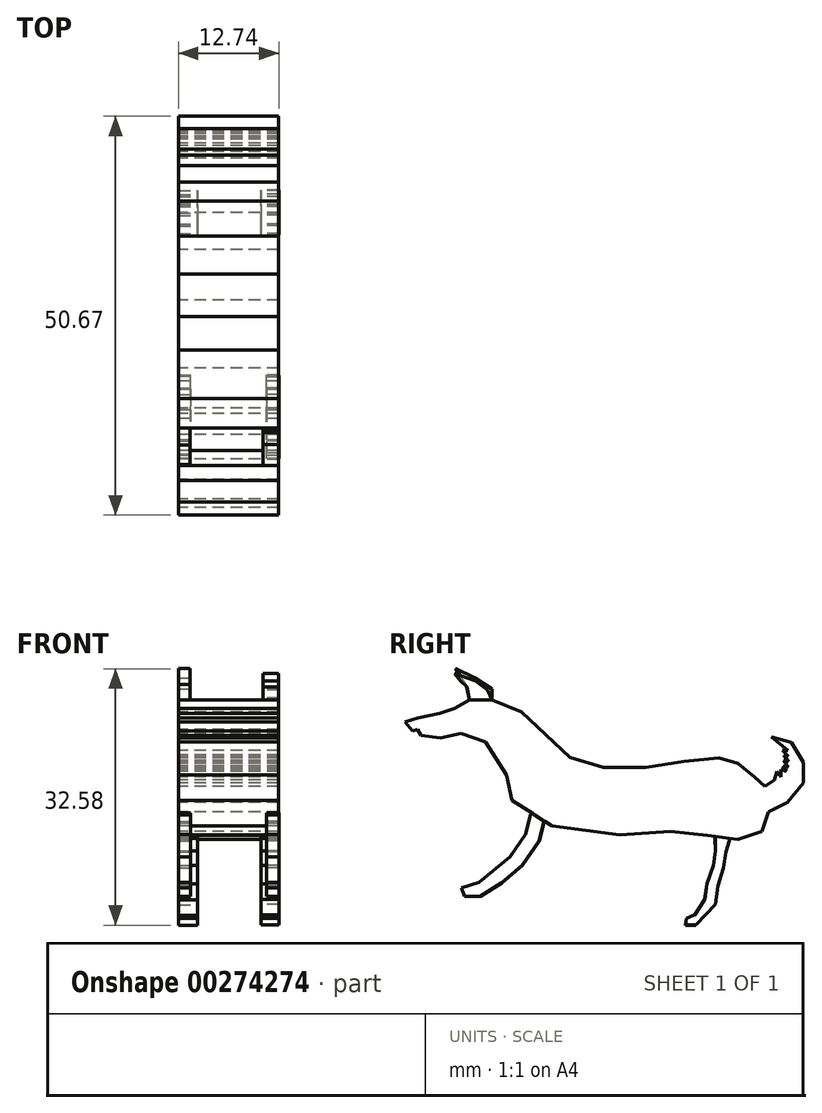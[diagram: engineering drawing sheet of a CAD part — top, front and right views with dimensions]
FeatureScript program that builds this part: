
annotation { "Feature Type Name" : "Feature", "Feature Type Description" : "" }
export const myFeature = defineFeature(function(context is Context, id is Id, definition is map)
    precondition{}
    {
        {
            var Q0;
            Q0=qCreatedBy(makeId("Right.planeOp"),FACE);
            var sketch = newSketch(context, id + "F0", { "sketchPlane" : qUnion([Q0])});
            skLineSegment(sketch, "E0", {"start": v(-9.66, 15.32) * mm, "end": v(-15.82, 21.1) * mm});
            skLineSegment(sketch, "E1", {"start": v(-15.82, 21.1) * mm, "end": v(-19.56, 22.63) * mm});
            skLineSegment(sketch, "E2", {"start": v(-22.42, 22.63) * mm, "end": v(-24.34, 21.56) * mm});
            skLineSegment(sketch, "E3", {"start": v(-24.34, 21.56) * mm, "end": v(-26.22, 20.93) * mm});
            skLineSegment(sketch, "E4", {"start": v(-26.22, 20.93) * mm, "end": v(-28.98, 20.37) * mm});
            skLineSegment(sketch, "E5", {"start": v(-28.98, 20.37) * mm, "end": v(-30.64, 19.86) * mm});
            skLineSegment(sketch, "E6", {"start": v(-30.64, 19.86) * mm, "end": v(-29.67, 18.72) * mm});
            skLineSegment(sketch, "E7", {"start": v(-29.67, 18.72) * mm, "end": v(-27.26, 19.22) * mm});
            skLineSegment(sketch, "E8", {"start": v(-27.26, 19.22) * mm, "end": v(-29, 18.85) * mm});
            skLineSegment(sketch, "E9", {"start": v(-29, 18.85) * mm, "end": v(-28.6, 18.11) * mm});
            skLineSegment(sketch, "E10", {"start": v(-28.6, 18.11) * mm, "end": v(-26.1, 17.83) * mm});
            skLineSegment(sketch, "E11", {"start": v(-26.1, 17.83) * mm, "end": v(-23.52, 18.38) * mm});
            skLineSegment(sketch, "E12", {"start": v(-23.52, 18.38) * mm, "end": v(-20.38, 17.27) * mm});
            skLineSegment(sketch, "E13", {"start": v(-20.38, 17.27) * mm, "end": v(-17.7, 13.09) * mm});
            skLineSegment(sketch, "E14", {"start": v(-17.7, 13.09) * mm, "end": v(-17.02, 9.88) * mm});
            skLineSegment(sketch, "E15", {"start": v(-17.02, 9.88) * mm, "end": v(-11.93, 6.63) * mm});
            skLineSegment(sketch, "E16", {"start": v(-11.93, 6.63) * mm, "end": v(-3.3, 5.48) * mm});
            skLineSegment(sketch, "E17", {"start": v(-3.3, 5.48) * mm, "end": v(3.1, 5.94) * mm});
            skLineSegment(sketch, "E18", {"start": v(3.1, 5.94) * mm, "end": v(7.78, 5.46) * mm});
            skLineSegment(sketch, "E19", {"start": v(7.78, 5.46) * mm, "end": v(11.67, 4.93) * mm});
            skLineSegment(sketch, "E20", {"start": v(11.67, 4.93) * mm, "end": v(14.7, 5.94) * mm});
            skLineSegment(sketch, "E21", {"start": v(14.7, 5.94) * mm, "end": v(15.56, 8.39) * mm});
            skLineSegment(sketch, "E22", {"start": v(15.56, 8.39) * mm, "end": v(17.97, 9.63) * mm});
            skLineSegment(sketch, "E23", {"start": v(17.97, 9.63) * mm, "end": v(20.03, 12.08) * mm});
            skLineSegment(sketch, "E24", {"start": v(20.03, 12.08) * mm, "end": v(20.03, 14.68) * mm});
            skLineSegment(sketch, "E25", {"start": v(20.03, 14.68) * mm, "end": v(18.45, 17.22) * mm});
            skLineSegment(sketch, "E26", {"start": v(18.45, 17.22) * mm, "end": v(15.9, 17.94) * mm});
            skLineSegment(sketch, "E27", {"start": v(15.9, 17.94) * mm, "end": v(18.01, 16.21) * mm});
            skLineSegment(sketch, "E28", {"start": v(18.01, 16.21) * mm, "end": v(17.35, 16.21) * mm});
            skLineSegment(sketch, "E29", {"start": v(17.35, 16.21) * mm, "end": v(18.12, 15.47) * mm});
            skLineSegment(sketch, "E30", {"start": v(18.12, 15.47) * mm, "end": v(17.54, 15.64) * mm});
            skLineSegment(sketch, "E31", {"start": v(17.54, 15.64) * mm, "end": v(18.12, 14.79) * mm});
            skLineSegment(sketch, "E32", {"start": v(18.12, 14.79) * mm, "end": v(17.46, 14.97) * mm});
            skLineSegment(sketch, "E33", {"start": v(17.46, 14.97) * mm, "end": v(18.09, 14.05) * mm});
            skLineSegment(sketch, "E34", {"start": v(18.09, 14.05) * mm, "end": v(17.4, 14.25) * mm});
            skLineSegment(sketch, "E35", {"start": v(17.4, 14.25) * mm, "end": v(17.85, 13.58) * mm});
            skLineSegment(sketch, "E36", {"start": v(17.85, 13.58) * mm, "end": v(17.12, 13.78) * mm});
            skLineSegment(sketch, "E37", {"start": v(17.12, 13.78) * mm, "end": v(17.12, 12.85) * mm});
            skLineSegment(sketch, "E38", {"start": v(17.12, 12.85) * mm, "end": v(16.63, 13.58) * mm});
            skLineSegment(sketch, "E39", {"start": v(16.63, 13.58) * mm, "end": v(16.31, 12.47) * mm});
            skLineSegment(sketch, "E40", {"start": v(16.31, 12.47) * mm, "end": v(15.9, 12.19) * mm});
            skLineSegment(sketch, "E41", {"start": v(15.9, 12.19) * mm, "end": v(15.12, 11.66) * mm});
            skLineSegment(sketch, "E42", {"start": v(15.12, 11.66) * mm, "end": v(13.8, 12.85) * mm});
            skLineSegment(sketch, "E43", {"start": v(13.8, 12.85) * mm, "end": v(11.66, 14.58) * mm});
            skLineSegment(sketch, "E44", {"start": v(11.66, 14.58) * mm, "end": v(9.24, 15.27) * mm});
            skLineSegment(sketch, "E45", {"start": v(9.24, 15.27) * mm, "end": v(4.8, 14.83) * mm});
            skLineSegment(sketch, "E46", {"start": v(4.8, 14.83) * mm, "end": v(0, 14.05) * mm});
            skLineSegment(sketch, "E47", {"start": v(0, 14.05) * mm, "end": v(-5.43, 14.05) * mm});
            skLineSegment(sketch, "E48", {"start": v(-5.43, 14.05) * mm, "end": v(-9.66, 15.32) * mm});
            skLineSegment(sketch, "E49", {"start": v(-19.56, 22.63) * mm, "end": v(-22.42, 22.63) * mm});
            skSolve(sketch);
        }
        {
            var Q0;
            Q0 = qSketchRegion(id + "F0", true);
            extrude(context, id + "F1", {"entities" : qUnion([Q0]), "depth" : 12.7 * mm, "offsetDistance" : 25.4 * mm});
        }
        {
            var Q0;
            Q0=makeQuery(id+"F1.opExtrude","SWEPT_FACE",FACE,{"disambiguationData":[OSD([sQuery(id+"F0.wireOp",EDGE,"E49")])]});
            var sketch = newSketch(context, id + "F2", { "sketchPlane" : qUnion([Q0])});
            skLineSegment(sketch, "E50.bottom", {"start": v(12.7, -19.56) * mm, "end": v(10.72, -19.56) * mm});
            skLineSegment(sketch, "E50.top", {"start": v(12.7, -22.42) * mm, "end": v(10.72, -22.42) * mm});
            skLineSegment(sketch, "E50.left", {"start": v(12.7, -19.56) * mm, "end": v(12.7, -22.42) * mm});
            skLineSegment(sketch, "E50.right", {"start": v(10.72, -19.56) * mm, "end": v(10.72, -22.42) * mm});
            skPoint(sketch, "E50.middle", {"position": v(11.7, -21) * mm});
            skPoint(sketch, "E50.middle.positionSnap0", {"position": v(12.7, -21) * mm});
            skPoint(sketch, "E50.centerSnap0", {"position": v(12.7, -21) * mm});
            skLineSegment(sketch, "E51.bottom", {"start": v(1.44, -19.56) * mm, "end": v(0.01, -19.56) * mm});
            skLineSegment(sketch, "E51.top", {"start": v(1.44, -22.42) * mm, "end": v(0.01, -22.42) * mm});
            skLineSegment(sketch, "E51.left", {"start": v(1.44, -19.56) * mm, "end": v(1.44, -22.42) * mm});
            skLineSegment(sketch, "E51.right", {"start": v(0.01, -19.56) * mm, "end": v(0.01, -22.42) * mm});
            skPoint(sketch, "E51.middle", {"position": v(0.72, -21) * mm});
            skPoint(sketch, "E51.middle.positionSnap0", {"position": v(0, -21) * mm});
            skPoint(sketch, "E51.centerSnap0", {"position": v(0, -21) * mm});
            skSolve(sketch);
        }
        {
            var Q0;
            Q0 = qSketchRegion(id + "F2", true);
            extrude(context, id + "F3", {"entities" : qUnion([Q0]), "operationType" : NewBodyOperationType.ADD, "depth" : 0.25 * mm, "offsetDistance" : 25.4 * mm});
        }
        {
            var Q0;
            Q0=makeQuery(id+"F3.opExtrude","SWEPT_FACE",FACE,{"disambiguationData":[OSD([sQuery(id+"F2.wireOp",EDGE,"E50.right")])]});
            var sketch = newSketch(context, id + "F4", { "sketchPlane" : qUnion([Q0])});
            skLineSegment(sketch, "E52", {"start": v(22.42, 22.63) * mm, "end": v(22.76, 24.29) * mm});
            skLineSegment(sketch, "E53", {"start": v(22.76, 24.29) * mm, "end": v(23.56, 25.07) * mm});
            skLineSegment(sketch, "E54", {"start": v(23.56, 25.07) * mm, "end": v(24.36, 25.99) * mm});
            skLineSegment(sketch, "E55", {"start": v(24.36, 25.99) * mm, "end": v(21.67, 25.07) * mm});
            skLineSegment(sketch, "E56", {"start": v(21.67, 25.07) * mm, "end": v(20.12, 23.91) * mm});
            skLineSegment(sketch, "E57", {"start": v(20.12, 23.91) * mm, "end": v(19.56, 22.63) * mm});
            skLineSegment(sketch, "E58", {"start": v(19.56, 22.63) * mm, "end": v(22.42, 22.63) * mm});
            skSolve(sketch);
        }
        {
            var Q0;
            Q0 = qSketchRegion(id + "F4", true);
            extrude(context, id + "F5", {"entities" : qUnion([Q0]), "operationType" : NewBodyOperationType.ADD, "oppositeDirection" : true, "depth" : 2 * mm, "offsetDistance" : 25.4 * mm});
        }
        {
            var Q0;
            Q0=makeQuery(id+"F3.opExtrude","SWEPT_FACE",FACE,{"disambiguationData":[OSD([sQuery(id+"F2.wireOp",EDGE,"E51.left")])]});
            var sketch = newSketch(context, id + "F6", { "sketchPlane" : qUnion([Q0])});
            skLineSegment(sketch, "E59", {"start": v(-19.56, 22.63) * mm, "end": v(-22.42, 22.63) * mm});
            skLineSegment(sketch, "E60", {"start": v(-22.42, 22.63) * mm, "end": v(-22.85, 24.57) * mm});
            skLineSegment(sketch, "E61", {"start": v(-22.85, 24.57) * mm, "end": v(-24.21, 26.6) * mm});
            skLineSegment(sketch, "E62", {"start": v(-24.21, 26.6) * mm, "end": v(-21.7, 25.42) * mm});
            skLineSegment(sketch, "E63", {"start": v(-21.7, 25.42) * mm, "end": v(-19.56, 24.02) * mm});
            skLineSegment(sketch, "E64", {"start": v(-19.56, 24.02) * mm, "end": v(-19.56, 22.63) * mm});
            skSolve(sketch);
        }
        {
            var Q0;
            Q0 = qSketchRegion(id + "F6", true);
            extrude(context, id + "F7", {"entities" : qUnion([Q0]), "operationType" : NewBodyOperationType.ADD, "oppositeDirection" : true, "depth" : 1.45 * mm, "offsetDistance" : 25.4 * mm});
        }
        {
            var Q0;
            Q0=makeQuery(id+"F1.opExtrude","SWEPT_FACE",FACE,{"disambiguationData":[OSD([sQuery(id+"F0.wireOp",EDGE,"E15")])]});
            var sketch = newSketch(context, id + "F8", { "sketchPlane" : qUnion([Q0])});
            skLineSegment(sketch, "E65.bottom", {"start": v(12.7, 16.64) * mm, "end": v(11.16, 16.64) * mm});
            skLineSegment(sketch, "E65.top", {"start": v(12.7, 14.69) * mm, "end": v(11.16, 14.69) * mm});
            skLineSegment(sketch, "E65.left", {"start": v(12.7, 16.64) * mm, "end": v(12.7, 14.69) * mm});
            skLineSegment(sketch, "E65.right", {"start": v(11.16, 16.64) * mm, "end": v(11.16, 14.69) * mm});
            skPoint(sketch, "E65.middle", {"position": v(11.93, 15.66) * mm});
            skLineSegment(sketch, "E66.bottom", {"start": v(0, 16.64) * mm, "end": v(2.4, 16.64) * mm});
            skLineSegment(sketch, "E66.top", {"start": v(0, 14.69) * mm, "end": v(2.4, 14.69) * mm});
            skLineSegment(sketch, "E66.left", {"start": v(0, 16.64) * mm, "end": v(0, 14.69) * mm});
            skLineSegment(sketch, "E66.right", {"start": v(1.52, 16.64) * mm, "end": v(1.52, 14.69) * mm});
            skPoint(sketch, "E66.middle", {"position": v(1.2, 15.66) * mm});
            skPoint(sketch, "E66.middle.positionSnap0", {"position": v(11.16, 15.66) * mm});
            skPoint(sketch, "E66.centerSnap0", {"position": v(11.16, 15.66) * mm});
            skSolve(sketch);
        }
        {
            var Q0;
            Q0 = qSketchRegion(id + "F8", true);
            extrude(context, id + "F9", {"entities" : qUnion([Q0]), "operationType" : NewBodyOperationType.ADD, "depth" : 0.25 * mm, "offsetDistance" : 25.4 * mm});
        }
        {
            var Q0;
            Q0=makeQuery(id+"F9.opExtrude","SWEPT_FACE",FACE,{"disambiguationData":[OSD([sQuery(id+"F8.wireOp",EDGE,"E66.right")])]});
            var sketch = newSketch(context, id + "F10", { "sketchPlane" : qUnion([Q0])});
            skLineSegment(sketch, "E67", {"start": v(-14.47, 8.25) * mm, "end": v(-12.82, 7.2) * mm});
            skLineSegment(sketch, "E68", {"start": v(-12.82, 7.2) * mm, "end": v(-12.96, 6.99) * mm});
            skLineSegment(sketch, "E69", {"start": v(-12.96, 6.99) * mm, "end": v(-14.61, 8.04) * mm});
            skLineSegment(sketch, "E70", {"start": v(-14.61, 8.04) * mm, "end": v(-14.47, 8.25) * mm});
            skLineSegment(sketch, "E71", {"start": v(-14.61, 8.04) * mm, "end": v(-15.29, 5.55) * mm});
            skLineSegment(sketch, "E72", {"start": v(-15.29, 5.55) * mm, "end": v(-17.25, 2.7) * mm});
            skLineSegment(sketch, "E73", {"start": v(-17.25, 2.7) * mm, "end": v(-19.58, 0.79) * mm});
            skLineSegment(sketch, "E74", {"start": v(-23.38, -1.23) * mm, "end": v(-22.99, -2.34) * mm});
            skLineSegment(sketch, "E75", {"start": v(-22.99, -2.34) * mm, "end": v(-21.03, -2.34) * mm});
            skLineSegment(sketch, "E76", {"start": v(-21.03, -2.34) * mm, "end": v(-18.32, -0.58) * mm});
            skLineSegment(sketch, "E77", {"start": v(-18.32, -0.58) * mm, "end": v(-15.72, 1.64) * mm});
            skLineSegment(sketch, "E78", {"start": v(-15.72, 1.64) * mm, "end": v(-13.54, 4.71) * mm});
            skLineSegment(sketch, "E79", {"start": v(-13.54, 4.71) * mm, "end": v(-12.96, 6.99) * mm});
            skLineSegment(sketch, "E80", {"start": v(-19.58, 0.79) * mm, "end": v(-21.2, -0.55) * mm});
            skLineSegment(sketch, "E81", {"start": v(-21.2, -0.55) * mm, "end": v(-23.38, -1.23) * mm});
            skSolve(sketch);
        }
        {
            var Q0;
            Q0 = qSketchRegion(id + "F10", true);
            extrude(context, id + "F11", {"entities" : qUnion([Q0]), "operationType" : NewBodyOperationType.ADD, "oppositeDirection" : true, "depth" : 1.52 * mm, "offsetDistance" : 25.4 * mm});
        }
        {
            var Q0;
            Q0=makeQuery(id+"F9.opExtrude","SWEPT_FACE",FACE,{"disambiguationData":[OSD([sQuery(id+"F8.wireOp",EDGE,"E65.right")])]});
            var sketch = newSketch(context, id + "F12", { "sketchPlane" : qUnion([Q0])});
            skLineSegment(sketch, "E82.MirrorCS", {"start": v(12.87, 7.2) * mm, "end": v(13, 6.99) * mm});
            skLineSegment(sketch, "E83.MirrorCS", {"start": v(14.66, 8.04) * mm, "end": v(14.52, 8.25) * mm});
            skLineSegment(sketch, "E84.MirrorCS", {"start": v(23.43, -1.24) * mm, "end": v(23.03, -2.34) * mm});
            skLineSegment(sketch, "E85.MirrorCS", {"start": v(14.52, 8.25) * mm, "end": v(12.87, 7.2) * mm});
            skLineSegment(sketch, "E86.MirrorCS", {"start": v(13, 6.99) * mm, "end": v(14.66, 8.04) * mm});
            skLineSegment(sketch, "E87.MirrorCS", {"start": v(14.66, 8.04) * mm, "end": v(15.33, 5.55) * mm});
            skLineSegment(sketch, "E88.MirrorCS", {"start": v(15.33, 5.55) * mm, "end": v(17.3, 2.7) * mm});
            skLineSegment(sketch, "E89.MirrorCS", {"start": v(17.3, 2.7) * mm, "end": v(19.63, 0.78) * mm});
            skLineSegment(sketch, "E90.MirrorCS", {"start": v(23.03, -2.34) * mm, "end": v(21.07, -2.34) * mm});
            skLineSegment(sketch, "E91.MirrorCS", {"start": v(21.07, -2.34) * mm, "end": v(18.37, -0.59) * mm});
            skLineSegment(sketch, "E92.MirrorCS", {"start": v(18.37, -0.59) * mm, "end": v(15.76, 1.64) * mm});
            skLineSegment(sketch, "E93.MirrorCS", {"start": v(15.76, 1.64) * mm, "end": v(13.58, 4.7) * mm});
            skLineSegment(sketch, "E94.MirrorCS", {"start": v(13.58, 4.7) * mm, "end": v(13, 6.99) * mm});
            skLineSegment(sketch, "E95.MirrorCS", {"start": v(21.24, -0.55) * mm, "end": v(23.43, -1.24) * mm});
            skLineSegment(sketch, "E96.MirrorCS", {"start": v(19.63, 0.78) * mm, "end": v(21.24, -0.55) * mm});
            skSolve(sketch);
        }
        {
            var Q0;
            Q0 = qSketchRegion(id + "F12", true);
            extrude(context, id + "F13", {"entities" : qUnion([Q0]), "operationType" : NewBodyOperationType.ADD, "oppositeDirection" : true, "depth" : 1.57 * mm, "offsetDistance" : 25.4 * mm});
        }
        {
            var Q0;
            Q0=makeQuery(id+"F1.opExtrude","SWEPT_FACE",FACE,{"disambiguationData":[OSD([sQuery(id+"F0.wireOp",EDGE,"E19")])]});
            var sketch = newSketch(context, id + "F14", { "sketchPlane" : qUnion([Q0])});
            skLineSegment(sketch, "E97.bottom", {"start": v(12.7, -9.85) * mm, "end": v(10.44, -9.85) * mm});
            skLineSegment(sketch, "E97.top", {"start": v(12.7, -8.03) * mm, "end": v(10.44, -8.03) * mm});
            skLineSegment(sketch, "E97.left", {"start": v(12.7, -9.85) * mm, "end": v(12.7, -8.03) * mm});
            skLineSegment(sketch, "E97.right", {"start": v(10.44, -9.85) * mm, "end": v(10.44, -8.03) * mm});
            skPoint(sketch, "E97.middle", {"position": v(11.57, -8.94) * mm});
            skPoint(sketch, "E97.middle.positionSnap0", {"position": v(12.7, -8.94) * mm});
            skPoint(sketch, "E97.centerSnap0", {"position": v(12.7, -8.94) * mm});
            skLineSegment(sketch, "E98.bottom", {"start": v(0, -9.83) * mm, "end": v(2.43, -9.83) * mm});
            skLineSegment(sketch, "E98.top", {"start": v(0, -8.05) * mm, "end": v(2.43, -8.05) * mm});
            skLineSegment(sketch, "E98.left", {"start": v(0, -9.83) * mm, "end": v(0, -8.05) * mm});
            skLineSegment(sketch, "E98.right", {"start": v(2.43, -9.83) * mm, "end": v(2.43, -8.05) * mm});
            skPoint(sketch, "E98.middle", {"position": v(1.21, -8.94) * mm});
            skPoint(sketch, "E98.middle.positionSnap0", {"position": v(0, -8.94) * mm});
            skPoint(sketch, "E98.centerSnap0", {"position": v(0, -8.94) * mm});
            skSolve(sketch);
        }
        {
            var Q0;
            Q0 = qSketchRegion(id + "F14", true);
            extrude(context, id + "F15", {"entities" : qUnion([Q0]), "operationType" : NewBodyOperationType.ADD, "depth" : 0.25 * mm, "offsetDistance" : 25.4 * mm});
        }
        {
            var Q0;
            Q0=makeQuery(id+"F15.opExtrude","SWEPT_FACE",FACE,{"disambiguationData":[OSD([sQuery(id+"F14.wireOp",EDGE,"E97.right")])]});
            var sketch = newSketch(context, id + "F16", { "sketchPlane" : qUnion([Q0])});
            skLineSegment(sketch, "E99", {"start": v(-8.8, 5.06) * mm, "end": v(-8.83, 5.31) * mm});
            skLineSegment(sketch, "E100", {"start": v(-8.83, 5.31) * mm, "end": v(-10.63, 5.07) * mm});
            skLineSegment(sketch, "E101", {"start": v(-10.63, 5.07) * mm, "end": v(-10.6, 4.82) * mm});
            skLineSegment(sketch, "E102", {"start": v(-10.6, 4.82) * mm, "end": v(-8.8, 5.06) * mm});
            skLineSegment(sketch, "E103", {"start": v(-8.8, 5.06) * mm, "end": v(-8.83, 3.48) * mm});
            skLineSegment(sketch, "E104", {"start": v(-8.83, 3.48) * mm, "end": v(-8.58, 1.63) * mm});
            skLineSegment(sketch, "E105", {"start": v(-8.58, 1.63) * mm, "end": v(-7.74, -0.72) * mm});
            skLineSegment(sketch, "E106", {"start": v(-7.74, -0.72) * mm, "end": v(-7.46, -2.72) * mm});
            skLineSegment(sketch, "E107", {"start": v(-7.46, -2.72) * mm, "end": v(-6.14, -4.7) * mm});
            skLineSegment(sketch, "E108", {"start": v(-6.14, -4.7) * mm, "end": v(-5.14, -5.12) * mm});
            skLineSegment(sketch, "E109", {"start": v(-5.14, -5.12) * mm, "end": v(-5.03, -5.96) * mm});
            skLineSegment(sketch, "E110", {"start": v(-5.03, -5.96) * mm, "end": v(-6.36, -5.96) * mm});
            skLineSegment(sketch, "E111", {"start": v(-6.36, -5.96) * mm, "end": v(-8.8, -3.36) * mm});
            skLineSegment(sketch, "E112", {"start": v(-8.8, -3.36) * mm, "end": v(-9.12, -0.98) * mm});
            skLineSegment(sketch, "E113", {"start": v(-9.12, -0.98) * mm, "end": v(-9.86, 1.28) * mm});
            skLineSegment(sketch, "E114", {"start": v(-9.86, 1.28) * mm, "end": v(-10.14, 3.33) * mm});
            skLineSegment(sketch, "E115", {"start": v(-10.14, 3.33) * mm, "end": v(-10.6, 4.82) * mm});
            skSolve(sketch);
        }
        {
            var Q0;
            Q0 = qSketchRegion(id + "F16", true);
            extrude(context, id + "F17", {"entities" : qUnion([Q0]), "operationType" : NewBodyOperationType.ADD, "oppositeDirection" : true, "depth" : 2.3 * mm, "offsetDistance" : 25.4 * mm});
        }
        {
            var Q0;
            Q0=makeQuery(id+"F15.opExtrude","SWEPT_FACE",FACE,{"disambiguationData":[OSD([sQuery(id+"F14.wireOp",EDGE,"E98.right")])]});
            var sketch = newSketch(context, id + "F18", { "sketchPlane" : qUnion([Q0])});
            skLineSegment(sketch, "E116.MirrorCS", {"start": v(8.77, 5.04) * mm, "end": v(8.8, 5.3) * mm});
            skLineSegment(sketch, "E117.MirrorCS", {"start": v(10.61, 5.05) * mm, "end": v(10.58, 4.8) * mm});
            skLineSegment(sketch, "E118.MirrorCS", {"start": v(5.12, -5.14) * mm, "end": v(5, -5.98) * mm});
            skLineSegment(sketch, "E119.MirrorCS", {"start": v(6.12, -4.72) * mm, "end": v(5.12, -5.14) * mm});
            skLineSegment(sketch, "E120.MirrorCS", {"start": v(10.12, 3.32) * mm, "end": v(10.58, 4.8) * mm});
            skLineSegment(sketch, "E121.MirrorCS", {"start": v(6.34, -5.98) * mm, "end": v(8.77, -3.38) * mm});
            skLineSegment(sketch, "E122.MirrorCS", {"start": v(5, -5.98) * mm, "end": v(6.34, -5.98) * mm});
            skLineSegment(sketch, "E123.MirrorCS", {"start": v(7.44, -2.74) * mm, "end": v(6.12, -4.72) * mm});
            skLineSegment(sketch, "E124.MirrorCS", {"start": v(7.72, -0.74) * mm, "end": v(7.44, -2.74) * mm});
            skLineSegment(sketch, "E125.MirrorCS", {"start": v(8.55, 1.62) * mm, "end": v(7.72, -0.74) * mm});
            skLineSegment(sketch, "E126.MirrorCS", {"start": v(8.8, 3.46) * mm, "end": v(8.55, 1.62) * mm});
            skLineSegment(sketch, "E127.MirrorCS", {"start": v(8.77, 5.04) * mm, "end": v(8.8, 3.46) * mm});
            skLineSegment(sketch, "E128.MirrorCS", {"start": v(10.58, 4.8) * mm, "end": v(8.77, 5.04) * mm});
            skLineSegment(sketch, "E129.MirrorCS", {"start": v(8.8, 5.3) * mm, "end": v(10.61, 5.05) * mm});
            skLineSegment(sketch, "E130.MirrorCS", {"start": v(9.84, 1.26) * mm, "end": v(10.12, 3.32) * mm});
            skLineSegment(sketch, "E131.MirrorCS", {"start": v(9.1, -1) * mm, "end": v(9.84, 1.26) * mm});
            skLineSegment(sketch, "E132.MirrorCS", {"start": v(8.77, -3.38) * mm, "end": v(9.1, -1) * mm});
            skSolve(sketch);
        }
        {
            var Q0;
            Q0 = qSketchRegion(id + "F18", true);
            extrude(context, id + "F19", {"entities" : qUnion([Q0]), "operationType" : NewBodyOperationType.ADD, "oppositeDirection" : true, "depth" : 2.44 * mm, "offsetDistance" : 25.4 * mm});
        }
    });
